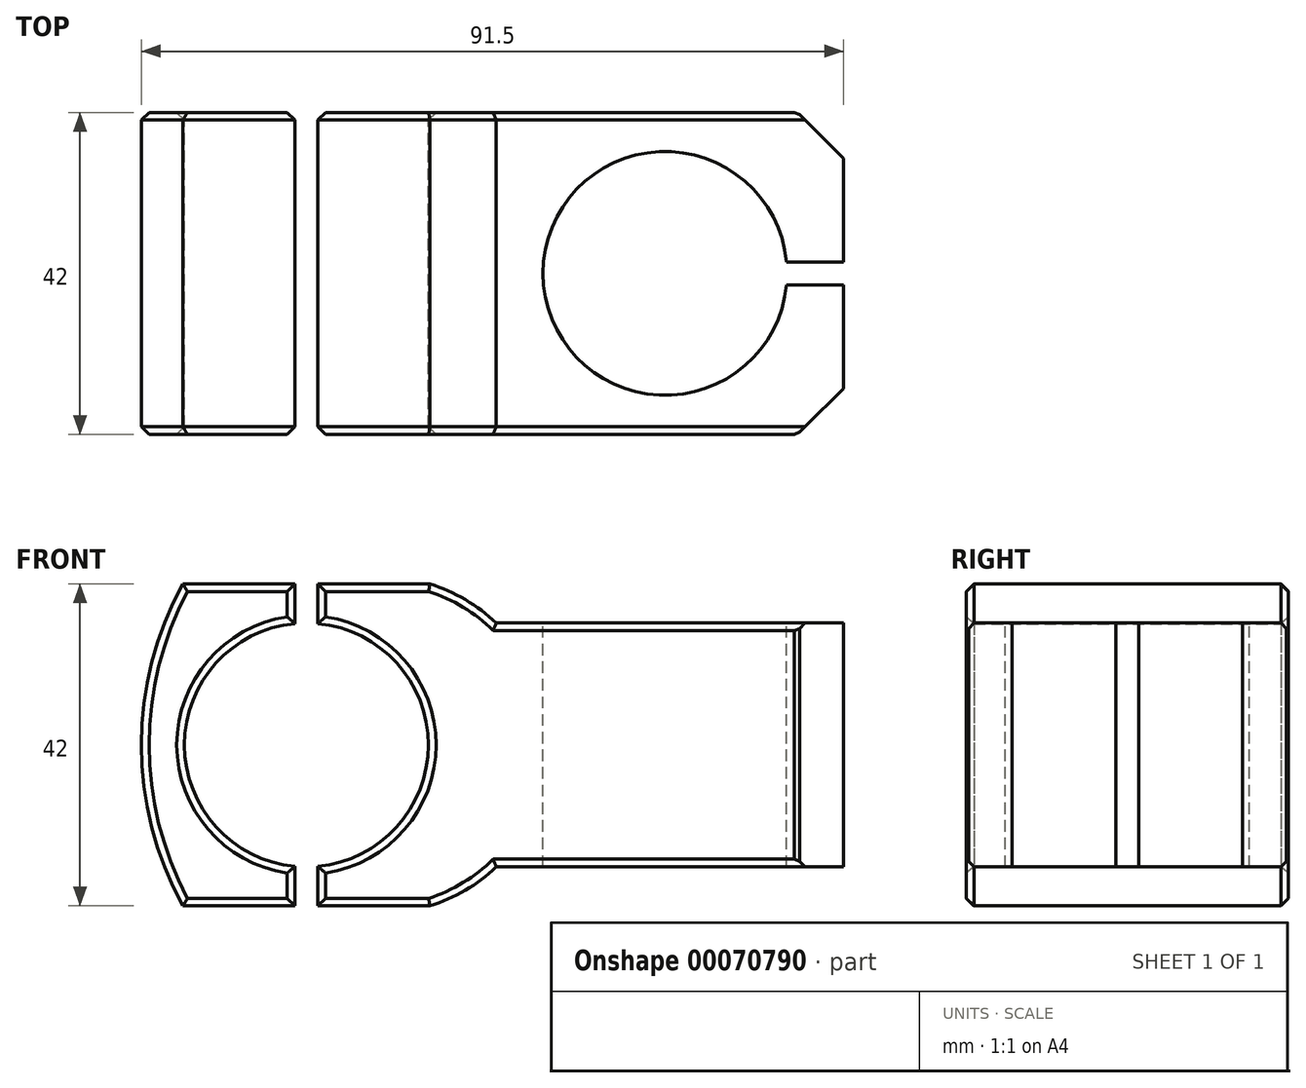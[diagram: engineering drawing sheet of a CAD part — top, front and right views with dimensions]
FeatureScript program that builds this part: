
annotation { "Feature Type Name" : "Feature", "Feature Type Description" : "" }
export const myFeature = defineFeature(function(context is Context, id is Id, definition is map)
    precondition{}
    {
        {
            var Q0;
            Q0=qCreatedBy(makeId("Front.planeOp"),FACE);
            var sketch = newSketch(context, id + "F0", { "sketchPlane" : qUnion([Q0])});
            skArc(sketch, "E0", {"start": v(-1.5, 15.83) * mm, "mid": v(-15.9, 0) * mm, "end": v(-1.5, -15.83) * mm});
            skArc(sketch, "E1", {"start": v(-16.1, 21) * mm, "mid": v(-21.5, 0) * mm, "end": v(-16.1, -21) * mm});
            skLineSegment(sketch, "E2.rect.bottom", {"start": v(-16.1, 21) * mm, "end": v(-1.5, 21) * mm});
            skLineSegment(sketch, "E2.rect.top", {"start": v(-16.1, -21) * mm, "end": v(-1.5, -21) * mm});
            skLineSegment(sketch, "E2.rect.right", {"start": v(70, 15.9) * mm, "end": v(70, -15.9) * mm});
            skPoint(sketch, "E2.rect.left.start.orphan", {"position": v(-26, 21) * mm});
            skPoint(sketch, "E3.orphan", {"position": v(-26, -21) * mm});
            skLineSegment(sketch, "E4.rect.left", {"start": v(-1.5, 21) * mm, "end": v(-1.5, 15.83) * mm});
            skLineSegment(sketch, "E4.rect.right", {"start": v(1.5, 21) * mm, "end": v(1.5, 15.83) * mm});
            skLineSegment(sketch, "E5.trimOffspring", {"start": v(1.5, 21) * mm, "end": v(16.1, 21) * mm});
            skLineSegment(sketch, "E6.trimOffspring", {"start": v(1.5, -15.83) * mm, "end": v(1.5, -21) * mm});
            skLineSegment(sketch, "E7.trimOffspring", {"start": v(-1.5, -15.83) * mm, "end": v(-1.5, -21) * mm});
            skArc(sketch, "E8.trimOffspring", {"start": v(1.5, -15.83) * mm, "mid": v(15.9, 0) * mm, "end": v(1.5, 15.83) * mm});
            skLineSegment(sketch, "E9.trimOffspring", {"start": v(1.5, -21) * mm, "end": v(16.1, -21) * mm});
            skLineSegment(sketch, "E10", {"start": v(24.74, 15.9) * mm, "end": v(70, 15.9) * mm});
            skLineSegment(sketch, "E11", {"start": v(70, -15.9) * mm, "end": v(24.74, -15.9) * mm});
            skArc(sketch, "E12.trimOffspring", {"start": v(16.1, -21) * mm, "mid": v(20.71, -18.95) * mm, "end": v(24.74, -15.9) * mm});
            skPoint(sketch, "E13.orphan", {"position": v(70, -21) * mm});
            skArc(sketch, "E14.trimOffspring", {"start": v(24.74, 15.9) * mm, "mid": v(20.71, 18.95) * mm, "end": v(16.1, 21) * mm});
            skPoint(sketch, "E15.orphan", {"position": v(70, 21) * mm});
            skSolve(sketch);
        }
        {
            var Q0;
            Q0 = qSketchRegion(id + "F0", true);
            extrude(context, id + "F1", {"entities" : qUnion([Q0]), "depth" : 42 * mm});
        }
        {
            var Q0;
            Q0=makeQuery(id+"F1.opExtrude","SWEPT_FACE",FACE,{"disambiguationData":[OSD([sQuery(id+"F0.wireOp",EDGE,"E10")])]});
            var sketch = newSketch(context, id + "F2", { "sketchPlane" : qUnion([Q0])});
            skArc(sketch, "E16", {"start": v(62.57, -19.5) * mm, "mid": v(30.84, -21) * mm, "end": v(62.57, -22.5) * mm});
            skPoint(sketch, "E16.centerSnap0", {"position": v(24.74, -21) * mm});
            skLineSegment(sketch, "E17", {"start": v(24.74, -21) * mm, "end": v(46.74, -21) * mm, "construction": true});
            skLineSegment(sketch, "E18", {"start": v(62.57, -19.5) * mm, "end": v(70, -19.5) * mm});
            skLineSegment(sketch, "E19", {"start": v(62.57, -22.5) * mm, "end": v(70, -22.5) * mm});
            skSolve(sketch);
        }
        {
            var Q0;
            Q0=makeQuery(id+"F2.imprint","IMPRINT",FACE,{"disambiguationData":[TD([[makeQuery(id+"F2.imprint","IMPRINT",EDGE,{"derivedFrom":sQuery(id+"F2.wireOp",EDGE,"E16")}),1.0]])]});
            extrude(context, id + "F3", {"entities" : qUnion([Q0]), "operationType" : NewBodyOperationType.REMOVE, "endBound" : BoundingType.THROUGH_ALL, "oppositeDirection" : true, "depth" : 25 * mm});
        }
        {
            var Q0;
            Q0=makeQuery(id+"F1.opExtrude","CAP_EDGE",EDGE,{"disambiguationData":[OSD([sQuery(id+"F0.wireOp",EDGE,"E2.rect.right")])],"isStart":false});
            var Q1;
            Q1=makeQuery(id+"F1.opExtrude","CAP_EDGE",EDGE,{"disambiguationData":[OSD([sQuery(id+"F0.wireOp",EDGE,"E2.rect.right")])],"isStart":true});
            chamfer(context, id + "F4", {"entities" : qUnion([Q0, Q1]), "width" : 6 * mm, "tangentPropagation" : true});
        }
        {
            var Q0;
            Q0=makeQuery(id+"F1.opExtrude","CAP_FACE",FACE,{"disambiguationData":[OSD([sQuery(id+"F0.wireOp",EDGE,"E2.rect.right"),sQuery(id+"F0.wireOp",EDGE,"E4.rect.right"),sQuery(id+"F0.wireOp",EDGE,"E5.trimOffspring"),sQuery(id+"F0.wireOp",EDGE,"E6.trimOffspring"),sQuery(id+"F0.wireOp",EDGE,"E8.trimOffspring"),sQuery(id+"F0.wireOp",EDGE,"E9.trimOffspring"),sQuery(id+"F0.wireOp",EDGE,"E10"),sQuery(id+"F0.wireOp",EDGE,"E11"),sQuery(id+"F0.wireOp",EDGE,"E12.trimOffspring"),sQuery(id+"F0.wireOp",EDGE,"E14.trimOffspring")])],"isStart":false});
            var Q1;
            Q1=makeQuery(id+"F1.opExtrude","CAP_FACE",FACE,{"disambiguationData":[OSD([sQuery(id+"F0.wireOp",EDGE,"E0"),sQuery(id+"F0.wireOp",EDGE,"E1"),sQuery(id+"F0.wireOp",EDGE,"E2.rect.bottom"),sQuery(id+"F0.wireOp",EDGE,"E2.rect.top"),sQuery(id+"F0.wireOp",EDGE,"E4.rect.left"),sQuery(id+"F0.wireOp",EDGE,"E7.trimOffspring")])],"isStart":false});
            var Q2;
            Q2=makeQuery(id+"F1.opExtrude","CAP_FACE",FACE,{"disambiguationData":[OSD([sQuery(id+"F0.wireOp",EDGE,"E2.rect.right"),sQuery(id+"F0.wireOp",EDGE,"E4.rect.right"),sQuery(id+"F0.wireOp",EDGE,"E5.trimOffspring"),sQuery(id+"F0.wireOp",EDGE,"E6.trimOffspring"),sQuery(id+"F0.wireOp",EDGE,"E8.trimOffspring"),sQuery(id+"F0.wireOp",EDGE,"E9.trimOffspring"),sQuery(id+"F0.wireOp",EDGE,"E10"),sQuery(id+"F0.wireOp",EDGE,"E11"),sQuery(id+"F0.wireOp",EDGE,"E12.trimOffspring"),sQuery(id+"F0.wireOp",EDGE,"E14.trimOffspring")])],"isStart":true});
            var Q3;
            Q3=makeQuery(id+"F1.opExtrude","CAP_FACE",FACE,{"disambiguationData":[OSD([sQuery(id+"F0.wireOp",EDGE,"E0"),sQuery(id+"F0.wireOp",EDGE,"E1"),sQuery(id+"F0.wireOp",EDGE,"E2.rect.bottom"),sQuery(id+"F0.wireOp",EDGE,"E2.rect.top"),sQuery(id+"F0.wireOp",EDGE,"E4.rect.left"),sQuery(id+"F0.wireOp",EDGE,"E7.trimOffspring")])],"isStart":true});
            chamfer(context, id + "F5", {"entities" : qUnion([Q0, Q1, Q2, Q3]), "width" : 1 * mm, "tangentPropagation" : true});
        }
    });
